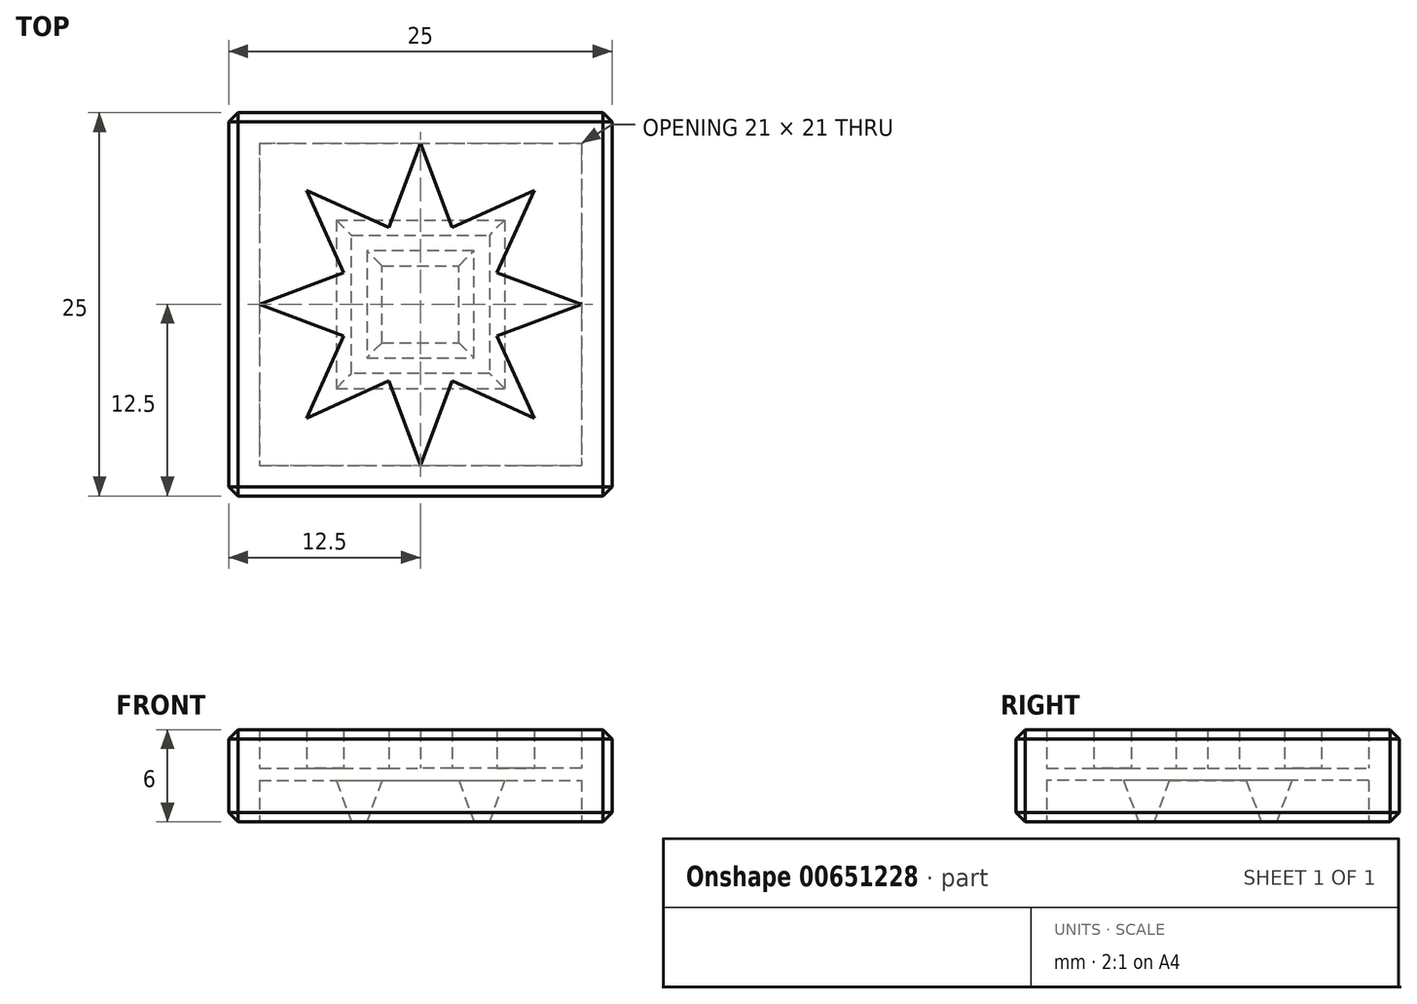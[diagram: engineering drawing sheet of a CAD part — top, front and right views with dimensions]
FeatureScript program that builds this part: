
annotation { "Feature Type Name" : "Feature", "Feature Type Description" : "" }
export const myFeature = defineFeature(function(context is Context, id is Id, definition is map)
    precondition{}
    {
        {
            var Q0;
            Q0=qCreatedBy(makeId("Top.planeOp"),FACE);
            var sketch = newSketch(context, id + "F0", { "sketchPlane" : qUnion([Q0])});
            skLineSegment(sketch, "E0.bottom", {"start": v(12.5, 12.5) * mm, "end": v(-12.5, 12.5) * mm});
            skLineSegment(sketch, "E0.top", {"start": v(12.5, -12.5) * mm, "end": v(-12.5, -12.5) * mm});
            skLineSegment(sketch, "E0.left", {"start": v(12.5, 12.5) * mm, "end": v(12.5, -12.5) * mm});
            skLineSegment(sketch, "E0.right", {"start": v(-12.5, 12.5) * mm, "end": v(-12.5, -12.5) * mm});
            skPoint(sketch, "E0.middle", {"position": v(0, 0) * mm});
            skCircle(sketch, "E1.cCircle", {"center": v(0, 0) * mm, "radius": 5 * mm, "construction": true});
            skLineSegment(sketch, "E1.6", {"start": v(-2.07, 5) * mm, "end": v(2.07, 5) * mm, "construction": true});
            skPoint(sketch, "E1.0.midPoint", {"position": v(5, 0) * mm});
            skLineSegment(sketch, "E2", {"start": v(-2.07, 5) * mm, "end": v(0, 10.5) * mm});
            skLineSegment(sketch, "E3", {"start": v(0, 10.5) * mm, "end": v(2.07, 5) * mm});
            skPoint(sketch, "E4.endSnap0", {"position": v(0, -8.67) * mm});
            skLineSegment(sketch, "E5", {"start": v(-2.07, 5) * mm, "end": v(0, 0) * mm, "construction": true});
            skLineSegment(sketch, "E6", {"start": v(2.07, 5) * mm, "end": v(0, 0) * mm, "construction": true});
            skPoint(sketch, "E7", {"position": v(0, 12.5) * mm});
            skLineSegment(sketch, "E8.1.0", {"start": v(-7.42, 7.42) * mm, "end": v(-2.07, 5) * mm});
            skLineSegment(sketch, "E8.1.1", {"start": v(-5, 2.07) * mm, "end": v(-7.42, 7.42) * mm});
            skLineSegment(sketch, "E8.2.0", {"start": v(-10.5, 0) * mm, "end": v(-5, 2.07) * mm});
            skLineSegment(sketch, "E8.2.1", {"start": v(-5, -2.07) * mm, "end": v(-10.5, 0) * mm});
            skLineSegment(sketch, "E8.3.0", {"start": v(-7.42, -7.42) * mm, "end": v(-5, -2.07) * mm});
            skLineSegment(sketch, "E8.3.1", {"start": v(-2.07, -5) * mm, "end": v(-7.42, -7.42) * mm});
            skLineSegment(sketch, "E8.4.0", {"start": v(0, -10.5) * mm, "end": v(-2.07, -5) * mm});
            skLineSegment(sketch, "E8.4.1", {"start": v(2.07, -5) * mm, "end": v(0, -10.5) * mm});
            skLineSegment(sketch, "E8.5.0", {"start": v(7.42, -7.42) * mm, "end": v(2.07, -5) * mm});
            skLineSegment(sketch, "E8.5.1", {"start": v(5, -2.07) * mm, "end": v(7.42, -7.42) * mm});
            skLineSegment(sketch, "E8.6.0", {"start": v(10.5, 0) * mm, "end": v(5, -2.07) * mm});
            skLineSegment(sketch, "E8.6.1", {"start": v(5, 2.07) * mm, "end": v(10.5, 0) * mm});
            skLineSegment(sketch, "E8.7.0", {"start": v(7.42, 7.42) * mm, "end": v(5, 2.07) * mm});
            skLineSegment(sketch, "E8.7.1", {"start": v(2.07, 5) * mm, "end": v(7.42, 7.42) * mm});
            skSolve(sketch);
        }
        {
            var Q0;
            Q0 = qSketchRegion(id + "F0", true);
            var Q1;
            Q1=makeQuery(id+"F0.imprint","IMPRINT",FACE,{"disambiguationData":[TD([[makeQuery(id+"F0.imprint","IMPRINT",EDGE,{"derivedFrom":sQuery(id+"F0.wireOp",EDGE,"E2")}),-1.0]])]});
            extrude(context, id + "F1", {"entities" : qUnion([Q0, Q1]), "depth" : 6 * mm, "offsetDistance" : 25 * mm});
        }
        {
            var Q0;
            Q0=qCreatedBy(makeId("Top.planeOp"),FACE);
            var sketch = newSketch(context, id + "F2", { "sketchPlane" : qUnion([Q0])});
            skLineSegment(sketch, "E9.bottom", {"start": v(-10.5, 10.5) * mm, "end": v(10.5, 10.5) * mm});
            skLineSegment(sketch, "E9.top", {"start": v(-10.5, -10.5) * mm, "end": v(10.5, -10.5) * mm});
            skLineSegment(sketch, "E9.left", {"start": v(-10.5, 10.5) * mm, "end": v(-10.5, -10.5) * mm});
            skLineSegment(sketch, "E9.right", {"start": v(10.5, 10.5) * mm, "end": v(10.5, -10.5) * mm});
            skPoint(sketch, "E9.middle", {"position": v(0, 0) * mm});
            skLineSegment(sketch, "E10.bottom", {"start": v(-5.5, 5.5) * mm, "end": v(5.5, 5.5) * mm});
            skLineSegment(sketch, "E10.top", {"start": v(-5.5, -5.5) * mm, "end": v(5.5, -5.5) * mm});
            skLineSegment(sketch, "E10.left", {"start": v(-5.5, 5.5) * mm, "end": v(-5.5, -5.5) * mm});
            skLineSegment(sketch, "E10.right", {"start": v(5.5, 5.5) * mm, "end": v(5.5, -5.5) * mm});
            skLineSegment(sketch, "E11.bottom", {"start": v(-2.5, -2.5) * mm, "end": v(2.5, -2.5) * mm});
            skLineSegment(sketch, "E11.top", {"start": v(-2.5, 2.5) * mm, "end": v(2.5, 2.5) * mm});
            skLineSegment(sketch, "E11.left", {"start": v(-2.5, -2.5) * mm, "end": v(-2.5, 2.5) * mm});
            skLineSegment(sketch, "E11.right", {"start": v(2.5, -2.5) * mm, "end": v(2.5, 2.5) * mm});
            skSolve(sketch);
        }
        {
            var Q0;
            Q0 = qSketchRegion(id + "F2", true);
            var Q1;
            Q1=makeQuery(id+"F2.imprint","IMPRINT",FACE,{"disambiguationData":[TD([[makeQuery(id+"F2.imprint","IMPRINT",EDGE,{"derivedFrom":sQuery(id+"F2.wireOp",EDGE,"E11.bottom")}),1.0]])]});
            extrude(context, id + "F3", {"entities" : qUnion([Q0, Q1]), "operationType" : NewBodyOperationType.REMOVE, "depth" : 2.7 * mm, "offsetDistance" : 25 * mm});
        }
        {
            var Q0;
            Q0=makeQuery(id+"F0.imprint","IMPRINT",FACE,{"disambiguationData":[TD([[makeQuery(id+"F0.imprint","IMPRINT",EDGE,{"derivedFrom":sQuery(id+"F0.wireOp",EDGE,"E2")}),-1.0]])]});
            extrude(context, id + "F4", {"entities" : qUnion([Q0]), "operationType" : NewBodyOperationType.REMOVE, "endBound" : BoundingType.THROUGH_ALL, "depth" : 25 * mm, "offsetDistance" : 25 * mm, "hasSecondDirection" : true, "secondDirectionOppositeDirection" : false, "secondDirectionDepth" : 3.5 * mm});
        }
        {
            var Q0;
            Q0=makeQuery(id+"F1.opExtrude","CAP_EDGE",EDGE,{"disambiguationData":[OSD([sQuery(id+"F0.wireOp",EDGE,"E0.top")])],"isStart":false});
            var Q1;
            Q1=makeQuery(id+"F1.opExtrude","SWEPT_EDGE",EDGE,{"disambiguationData":[OSD([sQuery(id+"F0.wireOp",EDGE,"E0.top"),sQuery(id+"F0.wireOp",EDGE,"E0.right")])]});
            var Q2;
            Q2=makeQuery(id+"F1.opExtrude","CAP_EDGE",EDGE,{"disambiguationData":[OSD([sQuery(id+"F0.wireOp",EDGE,"E0.right")])],"isStart":false});
            var Q3;
            Q3=makeQuery(id+"F1.opExtrude","SWEPT_EDGE",EDGE,{"disambiguationData":[OSD([sQuery(id+"F0.wireOp",EDGE,"E0.bottom"),sQuery(id+"F0.wireOp",EDGE,"E0.right")])]});
            var Q4;
            Q4=makeQuery(id+"F1.opExtrude","CAP_EDGE",EDGE,{"disambiguationData":[OSD([sQuery(id+"F0.wireOp",EDGE,"E0.bottom")])],"isStart":false});
            var Q5;
            Q5=makeQuery(id+"F1.opExtrude","CAP_EDGE",EDGE,{"disambiguationData":[OSD([sQuery(id+"F0.wireOp",EDGE,"E0.left")])],"isStart":false});
            var Q6;
            Q6=makeQuery(id+"F1.opExtrude","SWEPT_EDGE",EDGE,{"disambiguationData":[OSD([sQuery(id+"F0.wireOp",EDGE,"E0.top"),sQuery(id+"F0.wireOp",EDGE,"E0.left")])]});
            var Q7;
            Q7=makeQuery(id+"F1.opExtrude","SWEPT_EDGE",EDGE,{"disambiguationData":[OSD([sQuery(id+"F0.wireOp",EDGE,"E0.bottom"),sQuery(id+"F0.wireOp",EDGE,"E0.left")])]});
            var Q8;
            Q8=makeQuery(id+"F1.opExtrude","CAP_EDGE",EDGE,{"disambiguationData":[OSD([sQuery(id+"F0.wireOp",EDGE,"E0.top")])],"isStart":true});
            var Q9;
            Q9=makeQuery(id+"F1.opExtrude","CAP_EDGE",EDGE,{"disambiguationData":[OSD([sQuery(id+"F0.wireOp",EDGE,"E0.left")])],"isStart":true});
            var Q10;
            Q10=makeQuery(id+"F1.opExtrude","CAP_EDGE",EDGE,{"disambiguationData":[OSD([sQuery(id+"F0.wireOp",EDGE,"E0.bottom")])],"isStart":true});
            var Q11;
            Q11=makeQuery(id+"F1.opExtrude","CAP_EDGE",EDGE,{"disambiguationData":[OSD([sQuery(id+"F0.wireOp",EDGE,"E0.right")])],"isStart":true});
            chamfer(context, id + "F5", {"entities" : qUnion([Q0, Q1, Q2, Q3, Q4, Q5, Q6, Q7, Q8, Q9, Q10, Q11]), "width" : .6 * mm, "tangentPropagation" : true});
        }
        {
            var Q0;
            Q0=makeQuery(id+"F3.boolean.opBoolean","SPLIT",FACE,{"disambiguationData":[TD([makeQuery(id+"F3.opExtrude","SWEPT_FACE",FACE,{"disambiguationData":[OSD([sQuery(id+"F2.wireOp",EDGE,"E10.bottom")])]})])],"derivedFrom":makeQuery(id+"F1.opExtrude","CAP_FACE",FACE,{"disambiguationData":[OSD([sQuery(id+"F0.wireOp",EDGE,"E0.bottom"),sQuery(id+"F0.wireOp",EDGE,"E0.top"),sQuery(id+"F0.wireOp",EDGE,"E0.left"),sQuery(id+"F0.wireOp",EDGE,"E0.right")])],"isStart":true})});
            chamfer(context, id + "F6", {"entities" : qUnion([Q0]), "chamferType" : ChamferType.TWO_OFFSETS, "width1" : 1 * mm, "oppositeDirection" : false, "width2" : 2.7 * mm, "tangentPropagation" : true});
        }
    });
